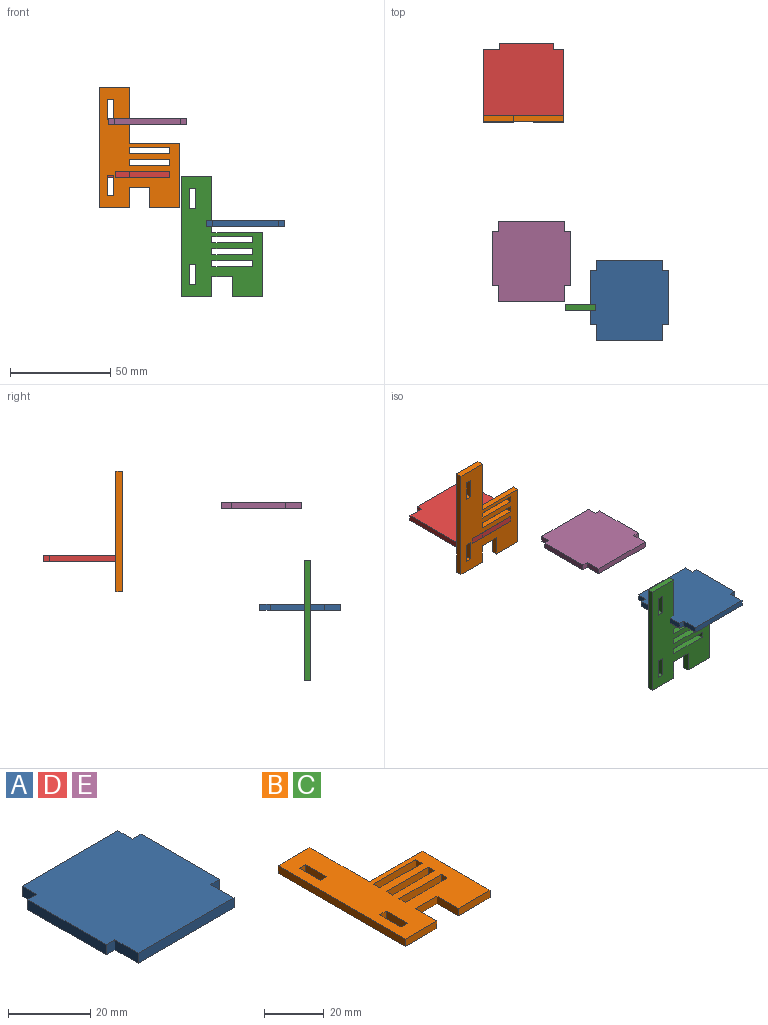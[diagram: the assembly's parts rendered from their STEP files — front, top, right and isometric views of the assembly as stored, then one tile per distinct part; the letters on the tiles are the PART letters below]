
ASSEMBLY  parts=5 mates=2
PART A: 14 faces, bbox 39x40x3 mm
  f0: plane 8x3mm, normal (-1,0,0), area 24mm2, adj f1,f11,f12,f13
  f1: plane 33x3mm, normal (0,-1,0), area 99mm2, adj f0,f2,f12,f13
  f2: plane 8x3mm, normal (1,0,0), area 24mm2, adj f1,f3,f12,f13
  f3: plane 3x3mm, normal (0,-1,0), area 9mm2, adj f2,f4,f12,f13
  f4: plane 27x3mm, normal (1,0,0), area 81mm2, adj f3,f5,f12,f13
  f5: plane 3x3mm, normal (0,1,0), area 9mm2, adj f4,f6,f12,f13
  f6: plane 5x3mm, normal (1,0,0), area 15mm2, adj f5,f7,f12,f13
  f7: plane 33x3mm, normal (0,1,0), area 99mm2, adj f6,f8,f12,f13
  f8: plane 5x3mm, normal (-1,0,0), area 15mm2, adj f7,f9,f12,f13
  f9: plane 3x3mm, normal (0,1,0), area 9mm2, adj f8,f10,f12,f13
  f10: plane 27x3mm, normal (-1,0,0), area 81mm2, adj f9,f11,f12,f13
  f11: plane 3x3mm, normal (0,-1,0), area 9mm2, adj f0,f10,f12,f13
  f12: plane 40x39mm, normal (0,0,1), area 1482mm2, adj f0,f1,f2,f3,f4,f5,f6,f7
  f13: plane 40x39mm, normal (0,0,-1), area 1482mm2, adj f0,f1,f2,f3,f4,f5,f6,f7
PART B: 32 faces, bbox 40x60x3 mm
  f0: plane 3x3mm, normal (0,1,0), area 9mm2, adj f1,f29,f30,f31
  f1: plane 10x3mm, normal (1,0,0), area 30mm2, adj f0,f2,f30,f31
  f2: plane 3x3mm, normal (0,-1,0), area 9mm2, adj f1,f29,f30,f31
  f3: plane 15x3mm, normal (0,-1,0), area 45mm2, adj f4,f24,f30,f31
  f4: plane 10x3mm, normal (1,0,0), area 30mm2, adj f3,f5,f30,f31
  f5: plane 10x3mm, normal (0,-1,0), area 30mm2, adj f4,f6,f30,f31
  f6: plane 10x3mm, normal (-1,0,0), area 30mm2, adj f5,f7,f30,f31
  f7: plane 15x3mm, normal (0,-1,0), area 45mm2, adj f6,f8,f30,f31
  f8: plane 32x3mm, normal (1,0,0), area 96mm2, adj f7,f9,f30,f31
  f9: plane 25x3mm, normal (0,1,0), area 75mm2, adj f8,f10,f30,f31
  f10: plane 28x3mm, normal (1,0,0), area 84mm2, adj f9,f11,f30,f31
  f11: plane 15x3mm, normal (0,1,0), area 45mm2, adj f10,f24,f30,f31
  f12: plane 3x3mm, normal (-1,0,0), area 9mm2, adj f13,f25,f30,f31
  f13: plane 20x3mm, normal (0,1,0), area 60mm2, adj f12,f14,f30,f31
  f14: plane 3x3mm, normal (1,0,0), area 9mm2, adj f13,f25,f30,f31
  f15: plane 3x3mm, normal (-1,0,0), area 9mm2, adj f16,f26,f30,f31
  f16: plane 20x3mm, normal (0,1,0), area 60mm2, adj f15,f17,f30,f31
  f17: plane 3x3mm, normal (1,0,0), area 9mm2, adj f16,f26,f30,f31
  f18: plane 3x3mm, normal (-1,0,0), area 9mm2, adj f19,f27,f30,f31
  f19: plane 20x3mm, normal (0,1,0), area 60mm2, adj f18,f20,f30,f31
  f20: plane 3x3mm, normal (1,0,0), area 9mm2, adj f19,f27,f30,f31
  f21: plane 10x3mm, normal (1,0,0), area 30mm2, adj f22,f28,f30,f31
  f22: plane 3x3mm, normal (0,-1,0), area 9mm2, adj f21,f23,f30,f31
  f23: plane 10x3mm, normal (-1,0,0), area 30mm2, adj f22,f28,f30,f31
  f24: plane 60x3mm, normal (-1,0,0), area 180mm2, adj f3,f11,f30,f31
  f25: plane 20x3mm, normal (0,-1,0), area 60mm2, adj f12,f14,f30,f31
  f26: plane 20x3mm, normal (0,-1,0), area 60mm2, adj f15,f17,f30,f31
  f27: plane 20x3mm, normal (0,-1,0), area 60mm2, adj f18,f20,f30,f31
  f28: plane 3x3mm, normal (0,1,0), area 9mm2, adj f21,f23,f30,f31
  f29: plane 10x3mm, normal (-1,0,0), area 30mm2, adj f0,f2,f30,f31
  f30: plane 60x40mm, normal (0,0,1), area 1360mm2, adj f0,f1,f2,f3,f4,f5,f6,f7
  f31: plane 60x40mm, normal (0,0,-1), area 1360mm2, adj f0,f1,f2,f3,f4,f5,f6,f7
PART C: same geometry as B
PART D: same geometry as A
PART E: same geometry as A
PLACE A t=(32.03,-81.54,-16.13)mm
PLACE B rot(axis=(1,0,0),90deg) t=(-20.95,10.33,23.17)mm
PLACE C rot(axis=(1,0,0),90deg) t=(20.27,-83.69,-21.28)mm
PLACE D rot(axis=(0,0,-1),90deg) t=(-20.95,26.83,8.17)mm
PLACE E t=(-17.09,-62.35,34.67)mm
MATE fastened B.f18 <-> B.f25  axis (-1,0,0) through (-5.95,8.83,9.67)mm
MATE fastened D.f5 <-> B.f18  axis (1,0,0) through (-5.95,8.83,9.67)mm
